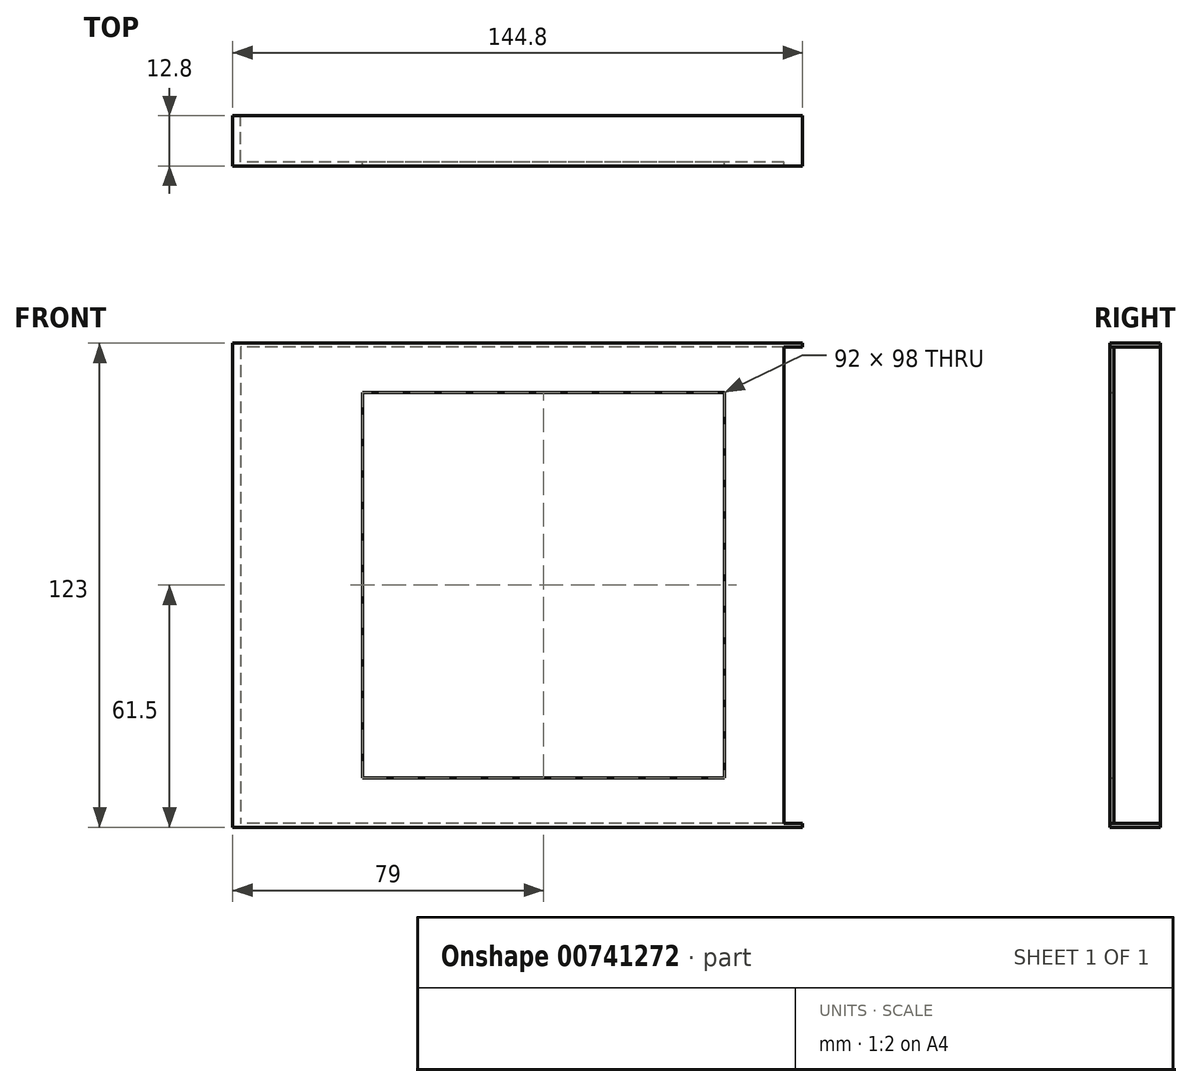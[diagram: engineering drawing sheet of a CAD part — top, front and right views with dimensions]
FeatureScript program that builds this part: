
annotation { "Feature Type Name" : "Feature", "Feature Type Description" : "" }
export const myFeature = defineFeature(function(context is Context, id is Id, definition is map)
    precondition{}
    {
        {
            var Q0;
            Q0=qCreatedBy(makeId("Front.planeOp"),FACE);
            var sketch = newSketch(context, id + "F0", { "sketchPlane" : qUnion([Q0])});
            skLineSegment(sketch, "E0.bottom", {"start": v(-74.5, -61.5) * mm, "end": v(65.5, -61.5) * mm});
            skLineSegment(sketch, "E0.top", {"start": v(-74.5, 61.5) * mm, "end": v(65.5, 61.5) * mm});
            skLineSegment(sketch, "E0.left", {"start": v(-74.5, -61.5) * mm, "end": v(-74.5, 61.5) * mm});
            skLineSegment(sketch, "E0.right", {"start": v(65.5, -61.5) * mm, "end": v(65.5, 61.5) * mm});
            skLineSegment(sketch, "E1.bottom", {"start": v(-41.5, 49) * mm, "end": v(50.5, 49) * mm});
            skLineSegment(sketch, "E1.top", {"start": v(-41.5, -49) * mm, "end": v(50.5, -49) * mm});
            skLineSegment(sketch, "E1.left", {"start": v(-41.5, 49) * mm, "end": v(-41.5, -49) * mm});
            skLineSegment(sketch, "E1.right", {"start": v(50.5, 49) * mm, "end": v(50.5, -49) * mm});
            skLineSegment(sketch, "E2.bottom", {"start": v(65.5, 60.5) * mm, "end": v(-72.5, 60.5) * mm});
            skLineSegment(sketch, "E2.top", {"start": v(65.5, -60.5) * mm, "end": v(-72.5, -60.5) * mm});
            skLineSegment(sketch, "E2.left", {"start": v(65.5, 60.5) * mm, "end": v(65.5, -60.5) * mm});
            skLineSegment(sketch, "E2.right", {"start": v(-72.5, 60.5) * mm, "end": v(-72.5, -60.5) * mm});
            skLineSegment(sketch, "E3.bottom", {"start": v(65.5, 61.5) * mm, "end": v(70.3, 61.5) * mm});
            skLineSegment(sketch, "E3.top", {"start": v(65.5, 60.5) * mm, "end": v(70.3, 60.5) * mm});
            skLineSegment(sketch, "E3.left", {"start": v(65.5, 61.5) * mm, "end": v(65.5, 60.5) * mm});
            skLineSegment(sketch, "E3.right", {"start": v(70.3, 61.5) * mm, "end": v(70.3, 60.5) * mm});
            skLineSegment(sketch, "E4.bottom", {"start": v(65.5, -60.5) * mm, "end": v(70.3, -60.5) * mm});
            skLineSegment(sketch, "E4.top", {"start": v(65.5, -61.5) * mm, "end": v(70.3, -61.5) * mm});
            skLineSegment(sketch, "E4.left", {"start": v(65.5, -60.5) * mm, "end": v(65.5, -61.5) * mm});
            skLineSegment(sketch, "E4.right", {"start": v(70.3, -60.5) * mm, "end": v(70.3, -61.5) * mm});
            skSolve(sketch);
        }
        {
            var Q0;
            {var subQ1=sQuery(id+"F0.wireOp",EDGE,"E0.bottom");Q0=makeQuery(id+"F0.imprint","IMPRINT",FACE,{"disambiguationData":[TD([[makeQuery(id+"F0.imprint","IMPRINT",EDGE,{"derivedFrom":subQ1}),1.0]])]});}
            var Q1;
            Q1=makeQuery(id+"F0.imprint","IMPRINT",FACE,{"disambiguationData":[TD([[makeQuery(id+"F0.imprint","IMPRINT",EDGE,{"derivedFrom":sQuery(id+"F0.wireOp",EDGE,"E1.bottom")}),-1.0]])]});
            var Q2;
            Q2=makeQuery(id+"F0.imprint","IMPRINT",FACE,{"disambiguationData":[TD([[makeQuery(id+"F0.imprint","IMPRINT",EDGE,{"derivedFrom":sQuery(id+"F0.wireOp",EDGE,"E1.bottom")}),1.0]])]});
            extrude(context, id + "F1", {"entities" : qUnion([Q0, Q1, Q2]), "depth" : 12.8 * mm, "offsetDistance" : 25 * mm});
        }
        {
            var Q0;
            Q0=makeQuery(id+"F0.imprint","IMPRINT",FACE,{"disambiguationData":[TD([[makeQuery(id+"F0.imprint","IMPRINT",EDGE,{"derivedFrom":sQuery(id+"F0.wireOp",EDGE,"E1.bottom")}),1.0]])]});
            var Q1;
            Q1=makeQuery(id+"F0.imprint","IMPRINT",FACE,{"disambiguationData":[TD([[makeQuery(id+"F0.imprint","IMPRINT",EDGE,{"derivedFrom":sQuery(id+"F0.wireOp",EDGE,"E1.bottom")}),-1.0]])]});
            extrude(context, id + "F2", {"entities" : qUnion([Q0, Q1]), "operationType" : NewBodyOperationType.REMOVE, "depth" : 11.8 * mm, "offsetDistance" : 25 * mm});
        }
        {
            var Q0;
            Q0=makeQuery(id+"F0.imprint","IMPRINT",FACE,{"disambiguationData":[TD([[makeQuery(id+"F0.imprint","IMPRINT",EDGE,{"derivedFrom":sQuery(id+"F0.wireOp",EDGE,"E1.bottom")}),-1.0]])]});
            extrude(context, id + "F3", {"entities" : qUnion([Q0]), "operationType" : NewBodyOperationType.REMOVE, "depth" : 12.8 * mm, "offsetDistance" : 25 * mm});
        }
        {
            var Q0;
            {var subQ0=sQuery(id+"F0.wireOp",EDGE,"E3.bottom");Q0=makeQuery(id+"F0.imprint","IMPRINT",FACE,{"disambiguationData":[TD([[makeQuery(id+"F0.imprint","IMPRINT",EDGE,{"derivedFrom":subQ0}),-1.0]])]});}
            var Q1;
            {var subQ2=sQuery(id+"F0.wireOp",EDGE,"E4.bottom");Q1=makeQuery(id+"F0.imprint","IMPRINT",FACE,{"disambiguationData":[TD([[makeQuery(id+"F0.imprint","IMPRINT",EDGE,{"derivedFrom":subQ2}),-1.0]])]});}
            extrude(context, id + "F4", {"entities" : qUnion([Q0, Q1]), "operationType" : NewBodyOperationType.ADD, "depth" : 12.8 * mm, "offsetDistance" : 25 * mm});
        }
    });
